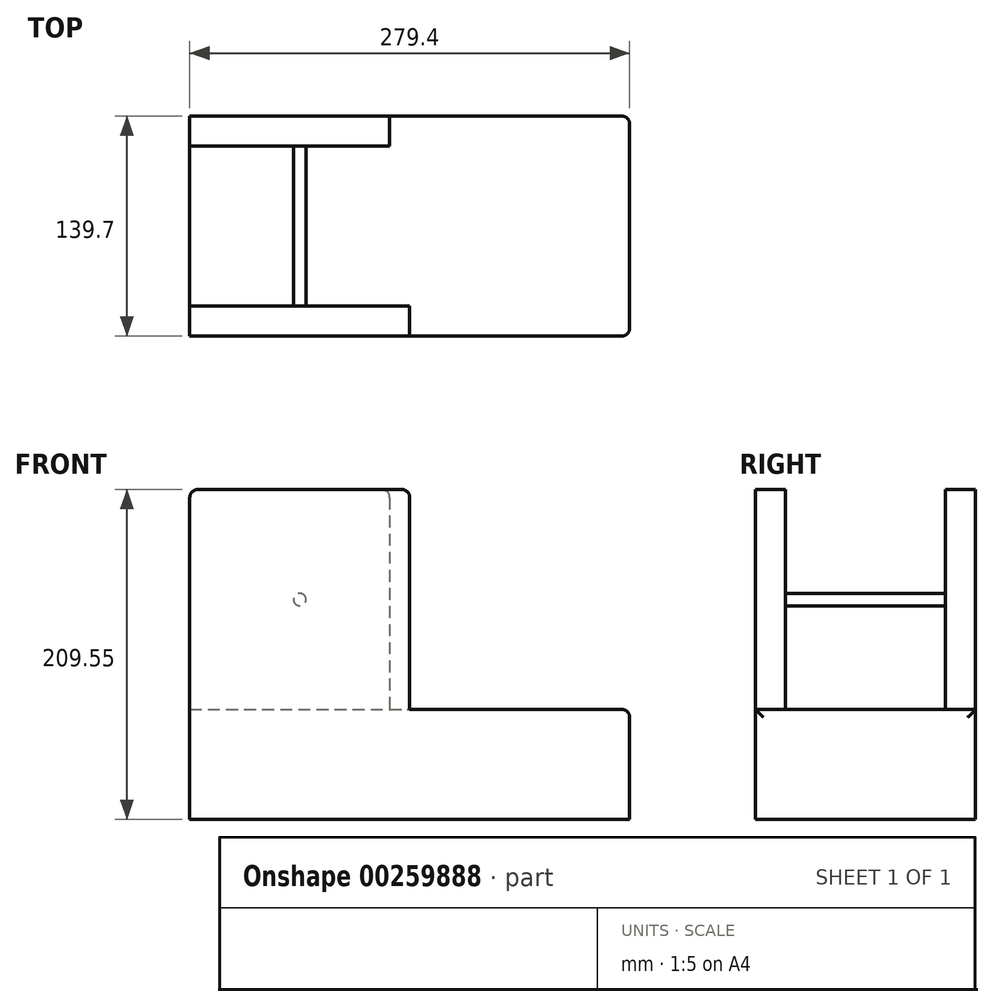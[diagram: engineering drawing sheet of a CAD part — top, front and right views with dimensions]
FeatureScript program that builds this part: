
annotation { "Feature Type Name" : "Feature", "Feature Type Description" : "" }
export const myFeature = defineFeature(function(context is Context, id is Id, definition is map)
    precondition{}
    {
        {
            var Q0;
            Q0=qCreatedBy(makeId("Top.planeOp"),FACE);
            var sketch = newSketch(context, id + "F0", { "sketchPlane" : qUnion([Q0])});
            skLineSegment(sketch, "E0.bottom", {"start": v(0, 0) * mm, "end": v(279.4, 0) * mm});
            skLineSegment(sketch, "E0.top", {"start": v(0, 139.7) * mm, "end": v(279.4, 139.7) * mm});
            skLineSegment(sketch, "E0.left", {"start": v(0, 0) * mm, "end": v(0, 139.7) * mm});
            skLineSegment(sketch, "E0.right", {"start": v(279.4, 0) * mm, "end": v(279.4, 139.7) * mm});
            skSolve(sketch);
        }
        {
            var Q0;
            Q0 = qSketchRegion(id + "F0", true);
            extrude(context, id + "F1", {"entities" : qUnion([Q0]), "depth" : 19.05 * mm});
        }
        {
            var Q0;
            Q0=makeQuery(id+"F1.opExtrude","CAP_FACE",FACE,{"disambiguationData":[OSD([sQuery(id+"F0.wireOp",EDGE,"E0.bottom"),sQuery(id+"F0.wireOp",EDGE,"E0.top"),sQuery(id+"F0.wireOp",EDGE,"E0.left"),sQuery(id+"F0.wireOp",EDGE,"E0.right")])],"isStart":false});
            var sketch = newSketch(context, id + "F2", { "sketchPlane" : qUnion([Q0])});
            skLineSegment(sketch, "E1.bottom", {"start": v(0, 139.7) * mm, "end": v(127, 139.7) * mm});
            skLineSegment(sketch, "E1.top", {"start": v(0, 120.65) * mm, "end": v(127, 120.65) * mm});
            skLineSegment(sketch, "E1.left", {"start": v(0, 139.7) * mm, "end": v(0, 120.65) * mm});
            skLineSegment(sketch, "E1.right", {"start": v(127, 139.7) * mm, "end": v(127, 120.65) * mm});
            skSolve(sketch);
        }
        {
            var Q0;
            Q0=makeQuery(id+"F2.imprint","IMPRINT",FACE,{"disambiguationData":[TD([[makeQuery(id+"F2.imprint","IMPRINT",EDGE,{"derivedFrom":sQuery(id+"F2.wireOp",EDGE,"E1.bottom")}),-1.0]])]});
            extrude(context, id + "F3", {"entities" : qUnion([Q0]), "operationType" : NewBodyOperationType.ADD, "depth" : 139.7 * mm});
        }
        {
            var Q0;
            Q0=makeQuery(id+"F1.opExtrude","CAP_FACE",FACE,{"disambiguationData":[OSD([sQuery(id+"F0.wireOp",EDGE,"E0.bottom"),sQuery(id+"F0.wireOp",EDGE,"E0.top"),sQuery(id+"F0.wireOp",EDGE,"E0.left"),sQuery(id+"F0.wireOp",EDGE,"E0.right")])],"isStart":false});
            var sketch = newSketch(context, id + "F4", { "sketchPlane" : qUnion([Q0])});
            skLineSegment(sketch, "E2.bottom", {"start": v(0, 0) * mm, "end": v(139.7, 0) * mm});
            skLineSegment(sketch, "E2.top", {"start": v(0, 19.05) * mm, "end": v(139.7, 19.05) * mm});
            skLineSegment(sketch, "E2.left", {"start": v(0, 0) * mm, "end": v(0, 19.05) * mm});
            skLineSegment(sketch, "E2.right", {"start": v(139.7, 0) * mm, "end": v(139.7, 19.05) * mm});
            skSolve(sketch);
        }
        {
            var Q0;
            Q0=makeQuery(id+"F4.imprint","IMPRINT",FACE,{"disambiguationData":[TD([[makeQuery(id+"F4.imprint","IMPRINT",EDGE,{"derivedFrom":sQuery(id+"F4.wireOp",EDGE,"E2.bottom")}),1.0]])]});
            extrude(context, id + "F5", {"entities" : qUnion([Q0]), "operationType" : NewBodyOperationType.ADD, "depth" : 139.7 * mm});
        }
        {
            var Q0;
            Q0=makeQuery(id+"F5.boolean.opBoolean","MERGE",FACE,{"derivedFrom":[makeQuery(id+"F1.opExtrude","SWEPT_FACE",FACE,{"disambiguationData":[OSD([sQuery(id+"F0.wireOp",EDGE,"E0.bottom")])]}),makeQuery(id+"F5.opExtrude","SWEPT_FACE",FACE,{"disambiguationData":[OSD([sQuery(id+"F4.wireOp",EDGE,"E2.bottom")])]})]});
            var sketch = newSketch(context, id + "F6", { "sketchPlane" : qUnion([Q0])});
            skCircle(sketch, "E3", {"center": v(69.85, 88.9) * mm, "radius": 3.97 * mm});
            skSolve(sketch);
        }
        {
            var Q0;
            Q0=makeQuery(id+"F6.imprint","IMPRINT",FACE,{"disambiguationData":[TD([[makeQuery(id+"F6.imprint","IMPRINT",EDGE,{"derivedFrom":sQuery(id+"F6.wireOp",EDGE,"E3")}),1.0]])]});
            var Q1;
            Q1=makeQuery(id+"F3.boolean.opBoolean","MERGE",FACE,{"derivedFrom":[makeQuery(id+"F1.opExtrude","SWEPT_FACE",FACE,{"disambiguationData":[OSD([sQuery(id+"F0.wireOp",EDGE,"E0.top")])]}),makeQuery(id+"F3.opExtrude","SWEPT_FACE",FACE,{"disambiguationData":[OSD([sQuery(id+"F2.wireOp",EDGE,"E1.bottom")])]})]});
            extrude(context, id + "F7", {"entities" : qUnion([Q0]), "operationType" : NewBodyOperationType.ADD, "endBound" : BoundingType.UP_TO_SURFACE, "oppositeDirection" : true, "endBoundEntityFace" : qUnion([Q1]), "depth" : 25.4 * mm});
        }
        {
            var Q0;
            Q0=makeQuery(id+"F5.opExtrude","CAP_EDGE",EDGE,{"disambiguationData":[OSD([sQuery(id+"F4.wireOp",EDGE,"E2.right")])],"isStart":false});
            var Q1;
            Q1=makeQuery(id+"F5.opExtrude","CAP_EDGE",EDGE,{"disambiguationData":[OSD([sQuery(id+"F4.wireOp",EDGE,"E2.left")])],"isStart":false});
            var Q2;
            Q2=makeQuery(id+"F3.opExtrude","CAP_EDGE",EDGE,{"disambiguationData":[OSD([sQuery(id+"F2.wireOp",EDGE,"E1.left")])],"isStart":false});
            var Q3;
            Q3=makeQuery(id+"F3.opExtrude","CAP_EDGE",EDGE,{"disambiguationData":[OSD([sQuery(id+"F2.wireOp",EDGE,"E1.right")])],"isStart":false});
            var Q4;
            Q4=makeQuery(id+"F1.opExtrude","SWEPT_EDGE",EDGE,{"disambiguationData":[OSD([sQuery(id+"F0.wireOp",EDGE,"E0.bottom"),sQuery(id+"F0.wireOp",EDGE,"E0.right")])]});
            var Q5;
            Q5=makeQuery(id+"F1.opExtrude","SWEPT_EDGE",EDGE,{"disambiguationData":[OSD([sQuery(id+"F0.wireOp",EDGE,"E0.top"),sQuery(id+"F0.wireOp",EDGE,"E0.right")])]});
            var Q6;
            Q6=makeQuery(id+"F1.opExtrude","CAP_EDGE",EDGE,{"disambiguationData":[OSD([sQuery(id+"F0.wireOp",EDGE,"E0.right")])],"isStart":false});
            fillet(context, id + "F8", {"entities" : qUnion([Q0, Q1, Q2, Q3, Q4, Q5, Q6]), "radius" : 5.08 * mm, "tangentPropagation" : true, "allowEdgeOverflow" : false});
        }
        {
            var Q0;
            Q0=makeQuery(id+"F1.opExtrude","CAP_FACE",FACE,{"disambiguationData":[OSD([sQuery(id+"F0.wireOp",EDGE,"E0.bottom"),sQuery(id+"F0.wireOp",EDGE,"E0.top"),sQuery(id+"F0.wireOp",EDGE,"E0.left"),sQuery(id+"F0.wireOp",EDGE,"E0.right")])],"isStart":true});
            extrude(context, id + "F9", {"entities" : qUnion([Q0]), "operationType" : NewBodyOperationType.ADD, "depth" : 50.8 * mm});
        }
    });
